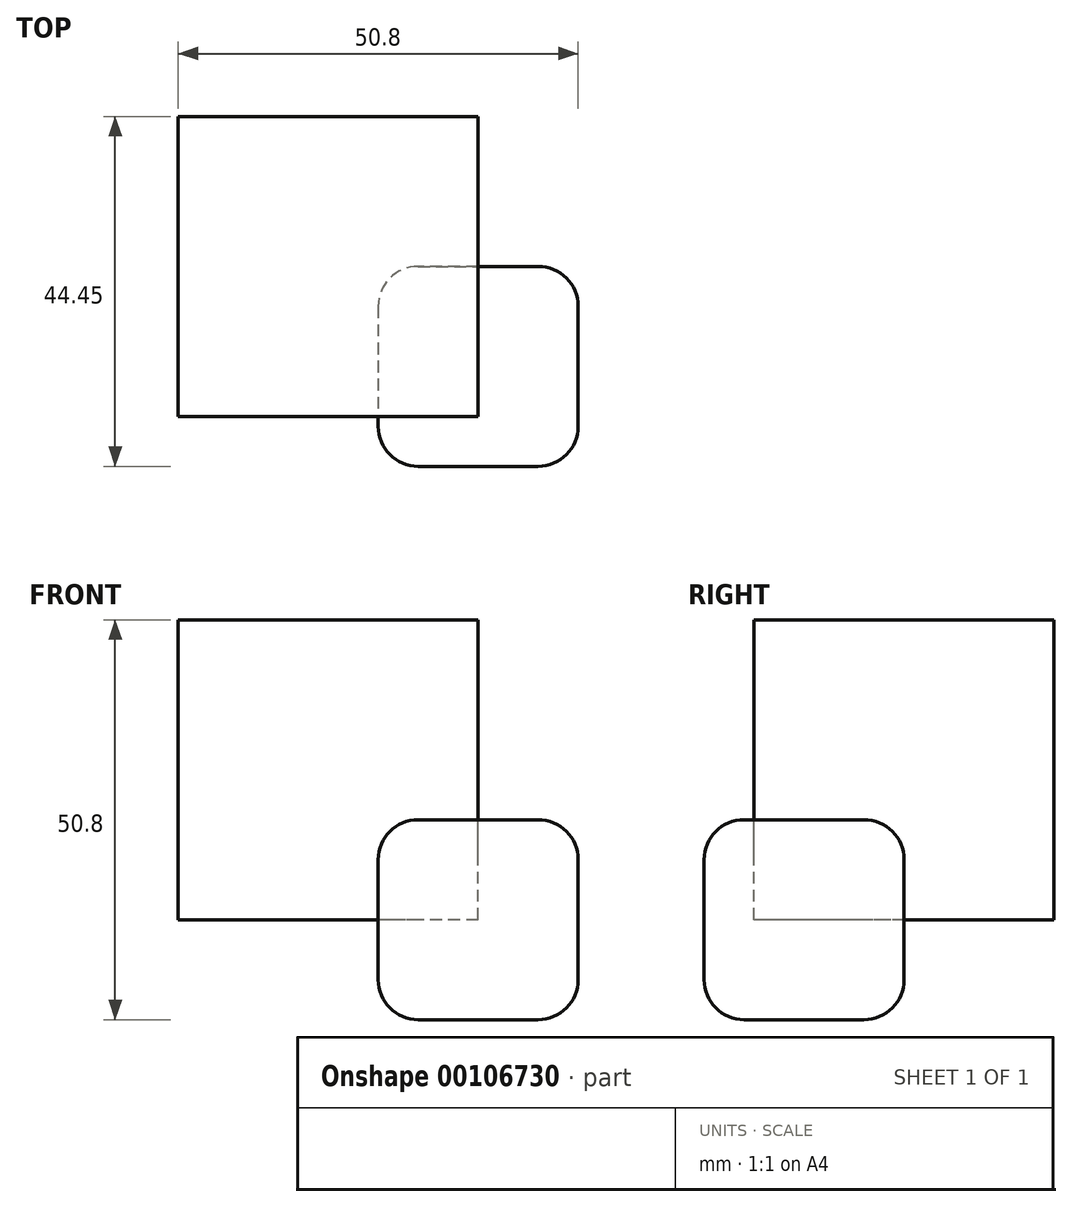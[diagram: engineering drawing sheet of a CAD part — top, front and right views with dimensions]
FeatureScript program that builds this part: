
annotation { "Feature Type Name" : "Feature", "Feature Type Description" : "" }
export const myFeature = defineFeature(function(context is Context, id is Id, definition is map)
    precondition{}
    {
        {
            var Q0;
            Q0=qCreatedBy(makeId("Front.planeOp"),FACE);
            var sketch = newSketch(context, id + "F0", { "sketchPlane" : qUnion([Q0])});
            skLineSegment(sketch, "E0.bottom", {"start": v(0, 0) * mm, "end": v(25.4, 0) * mm});
            skLineSegment(sketch, "E0.top", {"start": v(0, 25.4) * mm, "end": v(25.4, 25.4) * mm});
            skLineSegment(sketch, "E0.left", {"start": v(0, 0) * mm, "end": v(0, 25.4) * mm});
            skLineSegment(sketch, "E0.right", {"start": v(25.4, 0) * mm, "end": v(25.4, 25.4) * mm});
            skSolve(sketch);
        }
        {
            var Q0;
            Q0=makeQuery(id+"F0.imprint","IMPRINT",FACE,{"disambiguationData":[TD([[makeQuery(id+"F0.imprint","IMPRINT",EDGE,{"derivedFrom":sQuery(id+"F0.wireOp",EDGE,"E0.bottom")}),1.0]])]});
            extrude(context, id + "F1", {"entities" : qUnion([Q0]), "oppositeDirection" : true, "depth" : 25.4 * mm});
        }
        {
            var Q0;
            Q0=makeQuery(id+"F1.opExtrude","SWEPT_FACE",FACE,{"disambiguationData":[OSD([sQuery(id+"F0.wireOp",EDGE,"E0.top")])]});
            var Q1;
            Q1=makeQuery(id+"F1.opExtrude","CAP_FACE",FACE,{"disambiguationData":[OSD([sQuery(id+"F0.wireOp",EDGE,"E0.bottom"),sQuery(id+"F0.wireOp",EDGE,"E0.top"),sQuery(id+"F0.wireOp",EDGE,"E0.left"),sQuery(id+"F0.wireOp",EDGE,"E0.right")])],"isStart":true});
            var Q2;
            Q2=makeQuery(id+"F1.opExtrude","SWEPT_FACE",FACE,{"disambiguationData":[OSD([sQuery(id+"F0.wireOp",EDGE,"E0.right")])]});
            var Q3;
            Q3=makeQuery(id+"F1.opExtrude","SWEPT_FACE",FACE,{"disambiguationData":[OSD([sQuery(id+"F0.wireOp",EDGE,"E0.left")])]});
            var Q4;
            Q4=makeQuery(id+"F1.opExtrude","SWEPT_FACE",FACE,{"disambiguationData":[OSD([sQuery(id+"F0.wireOp",EDGE,"E0.bottom")])]});
            var Q5;
            Q5=makeQuery(id+"F1.opExtrude","CAP_FACE",FACE,{"disambiguationData":[OSD([sQuery(id+"F0.wireOp",EDGE,"E0.bottom"),sQuery(id+"F0.wireOp",EDGE,"E0.top"),sQuery(id+"F0.wireOp",EDGE,"E0.left"),sQuery(id+"F0.wireOp",EDGE,"E0.right")])],"isStart":false});
            fillet(context, id + "F2", {"entities" : qUnion([Q0, Q1, Q2, Q3, Q4, Q5]), "radius" : 5.08 * mm, "tangentPropagation" : true, "allowEdgeOverflow" : false});
        }
        {
            var Q0;
            Q0=makeQuery(id+"F1.opExtrude","CAP_FACE",FACE,{"disambiguationData":[OSD([sQuery(id+"F0.wireOp",EDGE,"E0.bottom"),sQuery(id+"F0.wireOp",EDGE,"E0.top"),sQuery(id+"F0.wireOp",EDGE,"E0.left"),sQuery(id+"F0.wireOp",EDGE,"E0.right")])],"isStart":false});
            var sketch = newSketch(context, id + "F3", { "sketchPlane" : qUnion([Q0])});
            skPoint(sketch, "E1.firstSnap0", {"position": v(-12.7, 20.32) * mm});
            skPoint(sketch, "E1.firstSnap1", {"position": v(-5.08, 12.7) * mm});
            skLineSegment(sketch, "E1.bottom", {"start": v(-12.7, 12.7) * mm, "end": v(25.4, 12.7) * mm});
            skLineSegment(sketch, "E1.top", {"start": v(-12.7, 50.8) * mm, "end": v(25.4, 50.8) * mm});
            skLineSegment(sketch, "E1.left", {"start": v(-12.7, 12.7) * mm, "end": v(-12.7, 50.8) * mm});
            skLineSegment(sketch, "E1.right", {"start": v(25.4, 12.7) * mm, "end": v(25.4, 50.8) * mm});
            skSolve(sketch);
        }
        {
            var Q0;
            {var subQ0=sQuery(id+"F3.wireOp",EDGE,"E1.left");var subQ1=sQuery(id+"F3.wireOp",EDGE,"E1.bottom");var subQ2=makeQuery(id+"F3.imprint","INTERSECT",VERTEX,{"derivedFrom":[subQ1,subQ0]});Q0=makeQuery(id+"F3.imprint","IMPRINT",FACE,{"disambiguationData":[TD([[makeQuery(id+"F3.imprint","IMPRINT",EDGE,{"disambiguationData":[TD([[subQ2,-1.0]])],"derivedFrom":subQ1}),1.0]])]});}
            var Q1;
            {var subQ1=sQuery(id+"F3.wireOp",EDGE,"E1.top");Q1=makeQuery(id+"F3.imprint","IMPRINT",FACE,{"disambiguationData":[TD([[makeQuery(id+"F3.imprint","IMPRINT",EDGE,{"derivedFrom":subQ1}),-1.0]])]});}
            extrude(context, id + "F4", {"entities" : qUnion([Q0, Q1]), "operationType" : NewBodyOperationType.ADD, "endBound" : BoundingType.SYMMETRIC, "depth" : 38.1 * mm});
        }
    });
